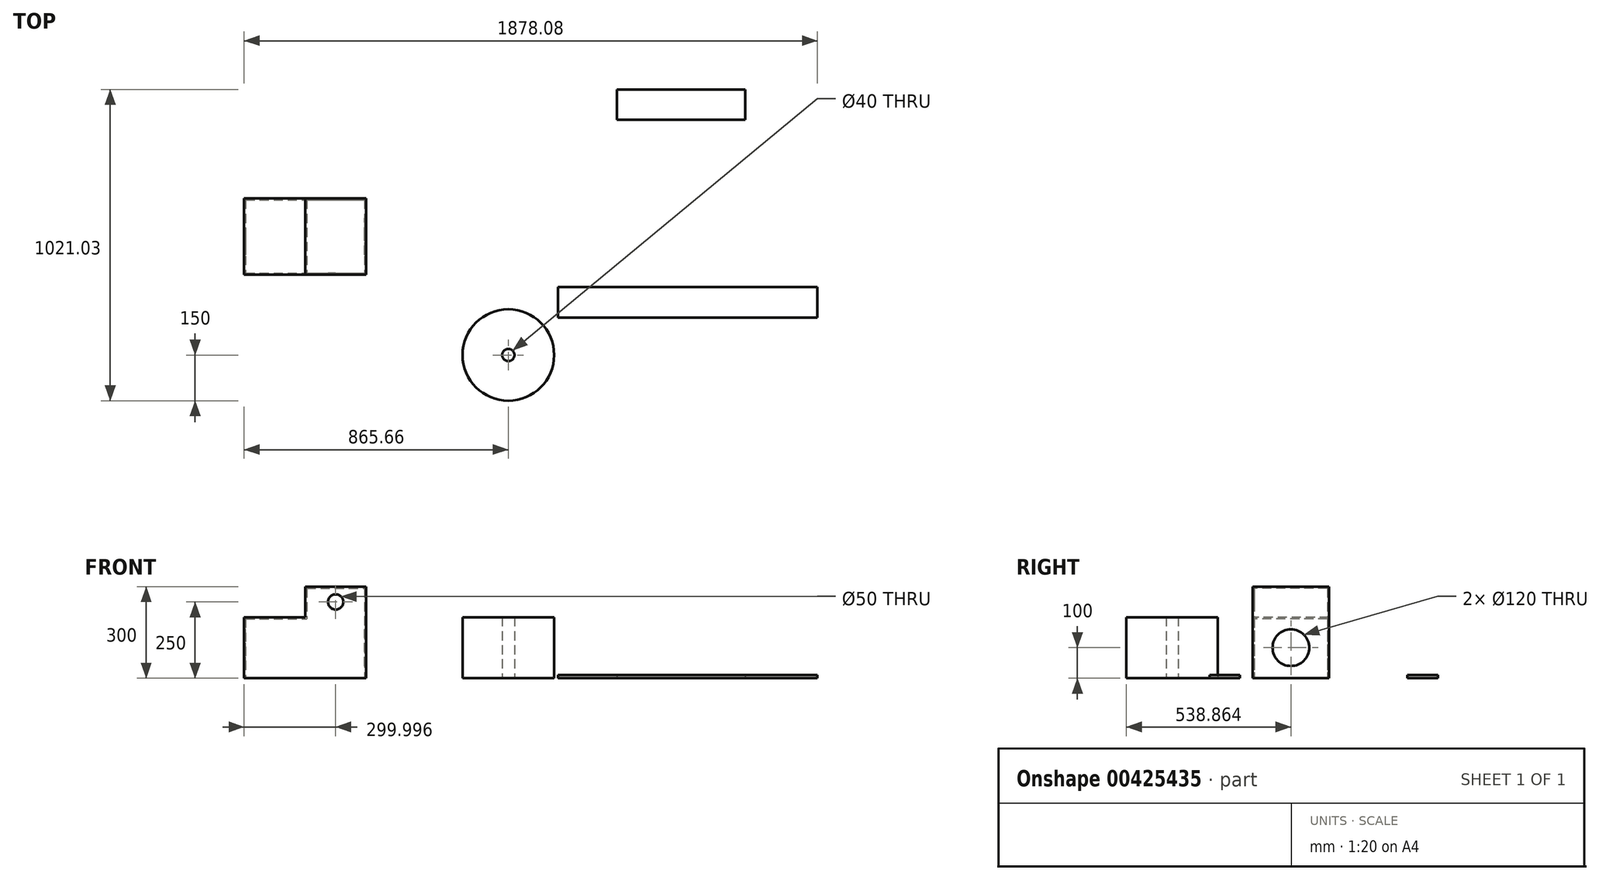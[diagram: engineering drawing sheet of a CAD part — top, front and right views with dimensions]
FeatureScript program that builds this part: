
annotation { "Feature Type Name" : "Feature", "Feature Type Description" : "" }
export const myFeature = defineFeature(function(context is Context, id is Id, definition is map)
    precondition{}
    {
        {
            var Q0;
            Q0=qCreatedBy(makeId("Top.planeOp"),FACE);
            var sketch = newSketch(context, id + "F0", { "sketchPlane" : qUnion([Q0])});
            skCircle(sketch, "E0", {"center": v(0, 0) * mm, "radius": 150 * mm});
            skCircle(sketch, "E1", {"center": v(0, 0) * mm, "radius": 20 * mm});
            skLineSegment(sketch, "E2", {"start": v(0, 0) * mm, "end": v(0, 150) * mm});
            skLineSegment(sketch, "E3", {"start": v(0, 0) * mm, "end": v(-20.88, 148.54) * mm});
            skSolve(sketch);
        }
        {
            var Q0;
            {var subQ0=sQuery(id+"F0.wireOp",EDGE,"E2");var subQ1=sQuery(id+"F0.wireOp",EDGE,"E0");var subQ2=makeQuery(id+"F0.imprint","INTERSECT",VERTEX,{"derivedFrom":[subQ1,subQ0]});Q0=makeQuery(id+"F0.imprint","IMPRINT",FACE,{"disambiguationData":[TD([[makeQuery(id+"F0.imprint","IMPRINT",EDGE,{"disambiguationData":[TD([[subQ2,1.0]])],"derivedFrom":subQ1}),1.0]])]});}
            var Q1;
            {var subQ0=sQuery(id+"F0.wireOp",EDGE,"E2");var subQ1=sQuery(id+"F0.wireOp",EDGE,"E0");var subQ2=makeQuery(id+"F0.imprint","INTERSECT",VERTEX,{"derivedFrom":[subQ1,subQ0]});Q1=makeQuery(id+"F0.imprint","IMPRINT",FACE,{"disambiguationData":[TD([[makeQuery(id+"F0.imprint","IMPRINT",EDGE,{"disambiguationData":[TD([[subQ2,-1.0]])],"derivedFrom":subQ1}),1.0]])]});}
            extrude(context, id + "F1", {"entities" : qUnion([Q0, Q1]), "depth" : 200 * mm});
        }
        {
            var Q0;
            Q0=qCreatedBy(makeId("Top.planeOp"),FACE);
            var sketch = newSketch(context, id + "F2", { "sketchPlane" : qUnion([Q0])});
            skLineSegment(sketch, "E4.bottom", {"start": v(162.42, 222.32) * mm, "end": v(1012.42, 222.32) * mm});
            skLineSegment(sketch, "E4.top", {"start": v(162.42, 122.32) * mm, "end": v(1012.42, 122.32) * mm});
            skLineSegment(sketch, "E4.left", {"start": v(162.42, 222.32) * mm, "end": v(162.42, 122.32) * mm});
            skLineSegment(sketch, "E4.right", {"start": v(1012.42, 222.32) * mm, "end": v(1012.42, 122.32) * mm});
            skSolve(sketch);
        }
        {
            var Q0;
            Q0=makeQuery(id+"F2.imprint","IMPRINT",FACE,{"disambiguationData":[TD([[makeQuery(id+"F2.imprint","IMPRINT",EDGE,{"derivedFrom":sQuery(id+"F2.wireOp",EDGE,"E4.bottom")}),-1.0]])]});
            extrude(context, id + "F3", {"entities" : qUnion([Q0]), "depth" : 10 * mm});
        }
        {
            var Q0;
            Q0=makeQuery(id+"F3.opExtrude","CAP_FACE",FACE,{"disambiguationData":[OSD([sQuery(id+"F2.wireOp",EDGE,"E4.bottom"),sQuery(id+"F2.wireOp",EDGE,"E4.top"),sQuery(id+"F2.wireOp",EDGE,"E4.left"),sQuery(id+"F2.wireOp",EDGE,"E4.right")])],"isStart":false});
            var sketch = newSketch(context, id + "F4", { "sketchPlane" : qUnion([Q0])});
            skLineSegment(sketch, "E5.bottom", {"start": v(182.42, 202.32) * mm, "end": v(202.42, 202.32) * mm});
            skLineSegment(sketch, "E5.top", {"start": v(182.42, 142.32) * mm, "end": v(202.42, 142.32) * mm});
            skLineSegment(sketch, "E5.left", {"start": v(182.42, 202.32) * mm, "end": v(182.42, 142.32) * mm});
            skLineSegment(sketch, "E5.right", {"start": v(202.42, 202.32) * mm, "end": v(202.42, 142.32) * mm});
            skLineSegment(sketch, "E6", {"start": v(182.42, 172.32) * mm, "end": v(1012.42, 172.32) * mm, "construction": true});
            skPoint(sketch, "E6.startSnap0", {"position": v(162.42, 172.32) * mm});
            skPoint(sketch, "E7", {"position": v(202.42, 172.32) * mm});
            skPoint(sketch, "E8", {"position": v(182.42, 172.32) * mm});
            skSolve(sketch);
        }
        {
            var Q0;
            Q0=qCreatedBy(makeId("Top.planeOp"),FACE);
            var sketch = newSketch(context, id + "F5", { "sketchPlane" : qUnion([Q0])});
            skLineSegment(sketch, "E9.bottom", {"start": v(-865.66, 513.86) * mm, "end": v(-465.66, 513.86) * mm});
            skLineSegment(sketch, "E9.top", {"start": v(-865.66, 263.86) * mm, "end": v(-465.66, 263.86) * mm});
            skLineSegment(sketch, "E9.left", {"start": v(-865.66, 513.86) * mm, "end": v(-865.66, 263.86) * mm});
            skLineSegment(sketch, "E9.right", {"start": v(-465.66, 513.86) * mm, "end": v(-465.66, 263.86) * mm});
            skSolve(sketch);
        }
        {
            var Q0;
            Q0=makeQuery(id+"F5.imprint","IMPRINT",FACE,{"disambiguationData":[TD([[makeQuery(id+"F5.imprint","IMPRINT",EDGE,{"derivedFrom":sQuery(id+"F5.wireOp",EDGE,"E9.bottom")}),-1.0]])]});
            extrude(context, id + "F6", {"entities" : qUnion([Q0]), "depth" : 200 * mm});
        }
        {
            var Q0;
            Q0=makeQuery(id+"F6.opExtrude","CAP_FACE",FACE,{"disambiguationData":[OSD([sQuery(id+"F5.wireOp",EDGE,"E9.bottom"),sQuery(id+"F5.wireOp",EDGE,"E9.top"),sQuery(id+"F5.wireOp",EDGE,"E9.left"),sQuery(id+"F5.wireOp",EDGE,"E9.right")])],"isStart":false});
            var sketch = newSketch(context, id + "F7", { "sketchPlane" : qUnion([Q0])});
            skLineSegment(sketch, "E10.bottom", {"start": v(-665.66, 513.86) * mm, "end": v(-465.66, 513.86) * mm});
            skLineSegment(sketch, "E10.top", {"start": v(-665.66, 263.86) * mm, "end": v(-465.66, 263.86) * mm});
            skLineSegment(sketch, "E10.left", {"start": v(-665.66, 513.86) * mm, "end": v(-665.66, 263.86) * mm});
            skLineSegment(sketch, "E10.right", {"start": v(-465.66, 513.86) * mm, "end": v(-465.66, 263.86) * mm});
            skLineSegment(sketch, "E11.bottom", {"start": v(-665.66, 388.86) * mm, "end": v(-465.66, 388.86) * mm});
            skLineSegment(sketch, "E11.left", {"start": v(-665.66, 388.86) * mm, "end": v(-665.66, 263.86) * mm});
            skLineSegment(sketch, "E11.right", {"start": v(-465.66, 388.86) * mm, "end": v(-465.66, 263.86) * mm});
            skSolve(sketch);
        }
        {
            var Q0;
            Q0=makeQuery(id+"F7.imprint","IMPRINT",FACE,{"disambiguationData":[TD([[makeQuery(id+"F7.imprint","IMPRINT",EDGE,{"derivedFrom":sQuery(id+"F7.wireOp",EDGE,"E11.bottom")}),-1.0]])]});
            var Q1;
            Q1=makeQuery(id+"F7.imprint","IMPRINT",FACE,{"disambiguationData":[TD([[makeQuery(id+"F7.imprint","IMPRINT",EDGE,{"derivedFrom":sQuery(id+"F7.wireOp",EDGE,"E10.bottom")}),-1.0]])]});
            extrude(context, id + "F8", {"entities" : qUnion([Q0, Q1]), "operationType" : NewBodyOperationType.ADD, "depth" : 100 * mm});
        }
        {
            var Q0;
            Q0=makeQuery(id+"F6.opExtrude","SWEPT_FACE",FACE,{"disambiguationData":[OSD([sQuery(id+"F5.wireOp",EDGE,"E9.left")])]});
            var sketch = newSketch(context, id + "F9", { "sketchPlane" : qUnion([Q0])});
            skCircle(sketch, "E12", {"center": v(-388.86, 100) * mm, "radius": 60 * mm});
            skSolve(sketch);
        }
        {
            var Q0;
            Q0=makeQuery(id+"F6.opExtrude","CAP_FACE",FACE,{"disambiguationData":[OSD([sQuery(id+"F5.wireOp",EDGE,"E9.bottom"),sQuery(id+"F5.wireOp",EDGE,"E9.top"),sQuery(id+"F5.wireOp",EDGE,"E9.left"),sQuery(id+"F5.wireOp",EDGE,"E9.right")])],"isStart":true});
            shell(context, id + "F10", {"entities" : qUnion([Q0]), "thickness" : 5 * mm});
        }
        {
            var Q0;
            Q0=makeQuery(id+"F9.imprint","IMPRINT",FACE,{"disambiguationData":[TD([[makeQuery(id+"F9.imprint","IMPRINT",EDGE,{"derivedFrom":sQuery(id+"F9.wireOp",EDGE,"E12")}),1.0]])]});
            extrude(context, id + "F11", {"entities" : qUnion([Q0]), "operationType" : NewBodyOperationType.REMOVE, "endBound" : BoundingType.THROUGH_ALL, "oppositeDirection" : true, "depth" : 25 * mm});
        }
        {
            var Q0;
            Q0=makeQuery(id+"F8.boolean.opBoolean","MERGE",FACE,{"derivedFrom":[makeQuery(id+"F6.opExtrude","SWEPT_FACE",FACE,{"disambiguationData":[OSD([sQuery(id+"F5.wireOp",EDGE,"E9.top")])]}),makeQuery(id+"F8.opExtrude","SWEPT_FACE",FACE,{"disambiguationData":[OSD([sQuery(id+"F7.wireOp",EDGE,"E10.top")])]})]});
            var sketch = newSketch(context, id + "F12", { "sketchPlane" : qUnion([Q0])});
            skCircle(sketch, "E13", {"center": v(-565.66, 250) * mm, "radius": 25 * mm});
            skSolve(sketch);
        }
        {
            var Q0;
            Q0=makeQuery(id+"F12.imprint","IMPRINT",FACE,{"disambiguationData":[TD([[makeQuery(id+"F12.imprint","IMPRINT",EDGE,{"derivedFrom":sQuery(id+"F12.wireOp",EDGE,"E13")}),1.0]])]});
            extrude(context, id + "F13", {"entities" : qUnion([Q0]), "operationType" : NewBodyOperationType.REMOVE, "oppositeDirection" : true, "depth" : 25 * mm});
        }
        {
            var Q0;
            Q0=qCreatedBy(makeId("Top.planeOp"),FACE);
            var sketch = newSketch(context, id + "F14", { "sketchPlane" : qUnion([Q0])});
            skLineSegment(sketch, "E14.bottom", {"start": v(355.5, 771.03) * mm, "end": v(775.5, 771.03) * mm});
            skLineSegment(sketch, "E14.top", {"start": v(355.5, 871.03) * mm, "end": v(775.5, 871.03) * mm});
            skLineSegment(sketch, "E14.left", {"start": v(355.5, 771.03) * mm, "end": v(355.5, 871.03) * mm});
            skLineSegment(sketch, "E14.right", {"start": v(775.5, 771.03) * mm, "end": v(775.5, 871.03) * mm});
            skSolve(sketch);
        }
        {
            var Q0;
            Q0=makeQuery(id+"F14.imprint","IMPRINT",FACE,{"disambiguationData":[TD([[makeQuery(id+"F14.imprint","IMPRINT",EDGE,{"derivedFrom":sQuery(id+"F14.wireOp",EDGE,"E14.bottom")}),1.0]])]});
            extrude(context, id + "F15", {"entities" : qUnion([Q0]), "depth" : 10 * mm});
        }
    });
